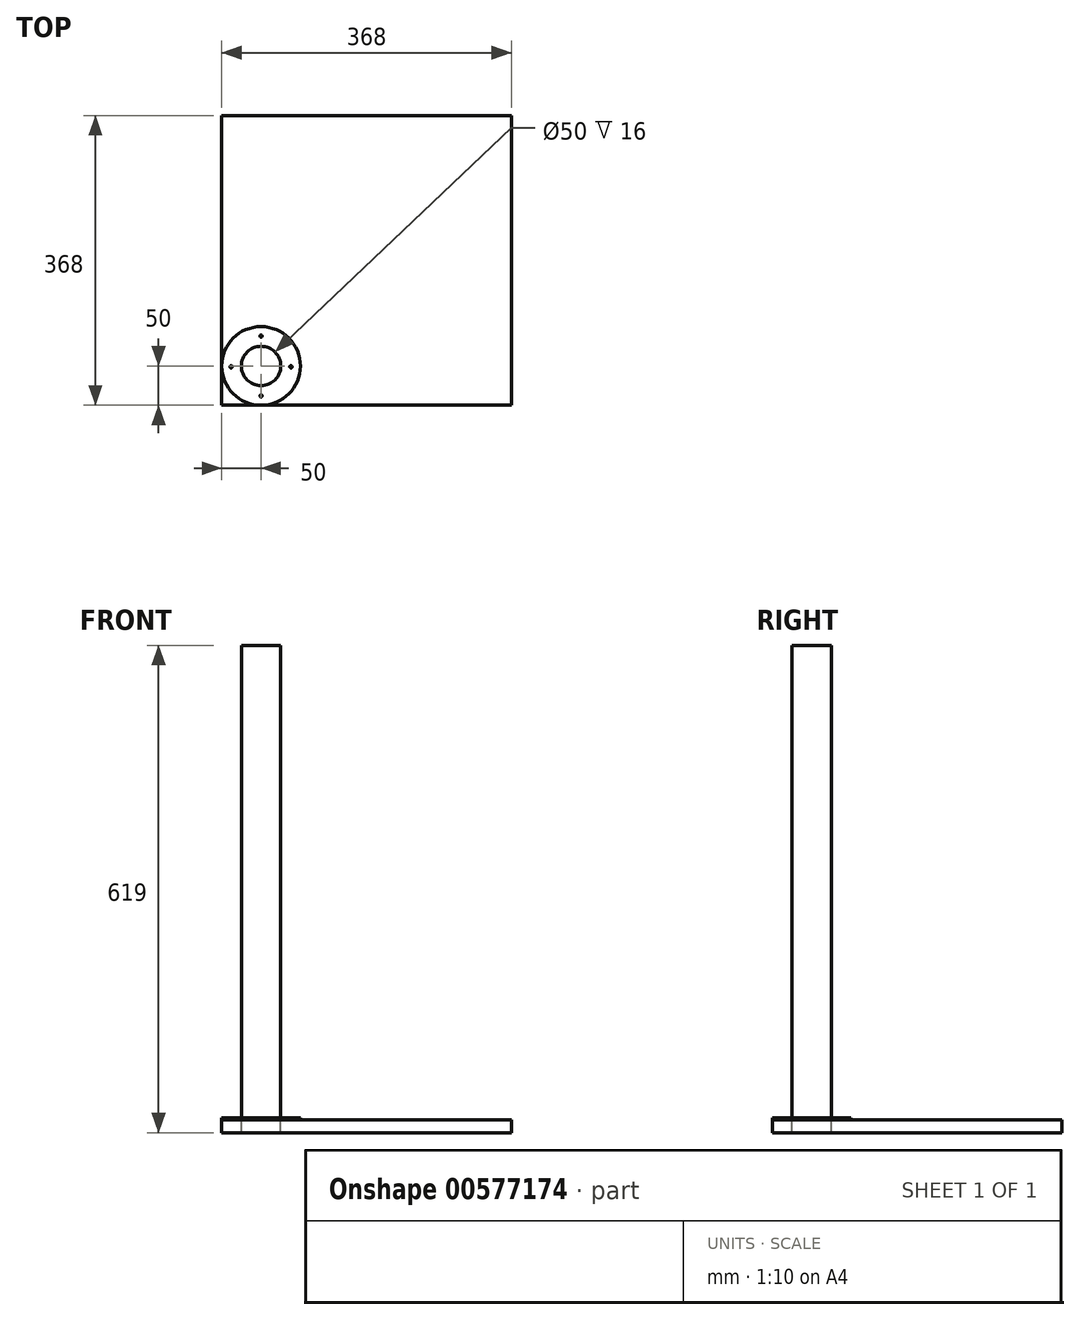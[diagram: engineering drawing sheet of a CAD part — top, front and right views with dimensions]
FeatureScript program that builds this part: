
annotation { "Feature Type Name" : "Feature", "Feature Type Description" : "" }
export const myFeature = defineFeature(function(context is Context, id is Id, definition is map)
    precondition{}
    {
        {
            var Q0;
            Q0=qCreatedBy(makeId("Top.planeOp"),FACE);
            var sketch = newSketch(context, id + "F0", { "sketchPlane" : qUnion([Q0])});
            skLineSegment(sketch, "E0.bottom", {"start": v(-184, 184) * mm, "end": v(184, 184) * mm});
            skLineSegment(sketch, "E0.top", {"start": v(-184, -184) * mm, "end": v(184, -184) * mm});
            skLineSegment(sketch, "E0.left", {"start": v(-184, 184) * mm, "end": v(-184, -184) * mm});
            skLineSegment(sketch, "E0.right", {"start": v(184, 184) * mm, "end": v(184, -184) * mm});
            skPoint(sketch, "E0.middle", {"position": v(0, 0) * mm});
            skPoint(sketch, "E1", {"position": v(-134, -134) * mm});
            skSolve(sketch);
        }
        {
            var Q0;
            Q0=makeQuery(id+"F0.imprint","IMPRINT",FACE,{"disambiguationData":[TD([[makeQuery(id+"F0.imprint","IMPRINT",EDGE,{"derivedFrom":sQuery(id+"F0.wireOp",EDGE,"E0.bottom")}),-1.0]])]});
            extrude(context, id + "F1", {"entities" : qUnion([Q0]), "depth" : 16 * mm, "offsetDistance" : 25 * mm});
        }
        {
            var Q0;
            Q0=makeQuery(id+"F1.opExtrude","CAP_FACE",FACE,{"disambiguationData":[OSD([sQuery(id+"F0.wireOp",EDGE,"E0.bottom"),sQuery(id+"F0.wireOp",EDGE,"E0.top"),sQuery(id+"F0.wireOp",EDGE,"E0.left"),sQuery(id+"F0.wireOp",EDGE,"E0.right")])],"isStart":false});
            var sketch = newSketch(context, id + "F2", { "sketchPlane" : qUnion([Q0])});
            skCircle(sketch, "E2", {"center": v(-134, -134) * mm, "radius": 50 * mm});
            skPoint(sketch, "E3", {"position": v(-96.02, -135.09) * mm});
            skPoint(sketch, "E4", {"position": v(-171.98, -135.09) * mm});
            skPoint(sketch, "E5", {"position": v(-134, -96) * mm});
            skPoint(sketch, "E6", {"position": v(-134, -172) * mm});
            skSolve(sketch);
        }
        {
            var Q0;
            Q0=sQuery(id+"F2.wireOp",VERTEX,"E2.center");
            var Q1;
            Q1=makeQuery(id+"F1.opExtrude","SWEPT_BODY",BODY,{"disambiguationData":[OSD([sQuery(id+"F0.wireOp",EDGE,"E0.bottom"),sQuery(id+"F0.wireOp",EDGE,"E0.top"),sQuery(id+"F0.wireOp",EDGE,"E0.left"),sQuery(id+"F0.wireOp",EDGE,"E0.right")])]});
            hole(context, id + "F3", {"style" : HoleStyle.SIMPLE, "endStyle" : HoleEndStyle.BLIND, "holeDiameter" : 50 * mm, "majorDiameter" : 5 * mm, "holeDepth" : 16 * mm, "isTappedThrough" : true, "tappedDepth" : 12 * mm, "tapClearance" : 3, "locations" : qUnion([Q0]), "scope" : qUnion([Q1])});
        }
        {
            var Q0;
            Q0 = qSketchRegion(id + "F2", true);
            extrude(context, id + "F4", {"entities" : qUnion([Q0]), "operationType" : NewBodyOperationType.ADD, "depth" : 3 * mm, "offsetDistance" : 25 * mm});
        }
        {
            var Q0;
            Q0=makeQuery(id+"F4.opExtrude","CAP_FACE",FACE,{"disambiguationData":[OSD([sQuery(id+"F2.wireOp",EDGE,"E2")])],"isStart":false});
            var sketch = newSketch(context, id + "F5", { "sketchPlane" : qUnion([Q0])});
            skCircle(sketch, "E7", {"center": v(-134, -134) * mm, "radius": 26 * mm});
            skSolve(sketch);
        }
        {
            var Q0;
            Q0=sQuery(id+"F5.wireOp",EDGE,"E7");
            extrude(context, id + "F6", {"bodyType" : ToolBodyType.SURFACE, "surfaceEntities" : qUnion([Q0]), "depth" : 200 * mm, "offsetDistance" : 25 * mm});
        }
        {
            var Q0;
            Q0=makeQuery(id+"F4.opExtrude","CAP_FACE",FACE,{"disambiguationData":[OSD([sQuery(id+"F2.wireOp",EDGE,"E2")])],"isStart":false});
            var sketch = newSketch(context, id + "F7", { "sketchPlane" : qUnion([Q0])});
            skCircle(sketch, "E8", {"center": v(-134, -134) * mm, "radius": 25 * mm});
            skSolve(sketch);
        }
        {
            var Q0;
            Q0 = qSketchRegion(id + "F7", true);
            extrude(context, id + "F8", {"entities" : qUnion([Q0]), "operationType" : NewBodyOperationType.ADD, "depth" : 600 * mm, "offsetDistance" : 25 * mm});
        }
        {
            var Q0;
            Q0=sQuery(id+"F2.wireOp",VERTEX,"E5");
            var Q1;
            Q1=sQuery(id+"F2.wireOp",VERTEX,"E4");
            var Q2;
            Q2=sQuery(id+"F2.wireOp",VERTEX,"E3");
            var Q3;
            Q3=sQuery(id+"F2.wireOp",VERTEX,"E6");
            var Q4;
            Q4=makeQuery(id+"F1.opExtrude","SWEPT_BODY",BODY,{"disambiguationData":[OSD([sQuery(id+"F0.wireOp",EDGE,"E0.bottom"),sQuery(id+"F0.wireOp",EDGE,"E0.top"),sQuery(id+"F0.wireOp",EDGE,"E0.left"),sQuery(id+"F0.wireOp",EDGE,"E0.right")])]});
            hole(context, id + "F9", {"style" : HoleStyle.SIMPLE, "endStyle" : HoleEndStyle.BLIND, "oppositeDirection" : true, "holeDiameter" : 3 * mm, "majorDiameter" : 5 * mm, "holeDepth" : 3 * mm, "isTappedThrough" : true, "tappedDepth" : 12 * mm, "tapClearance" : 3, "locations" : qUnion([Q0, Q1, Q2, Q3]), "scope" : qUnion([Q4])});
        }
    });
